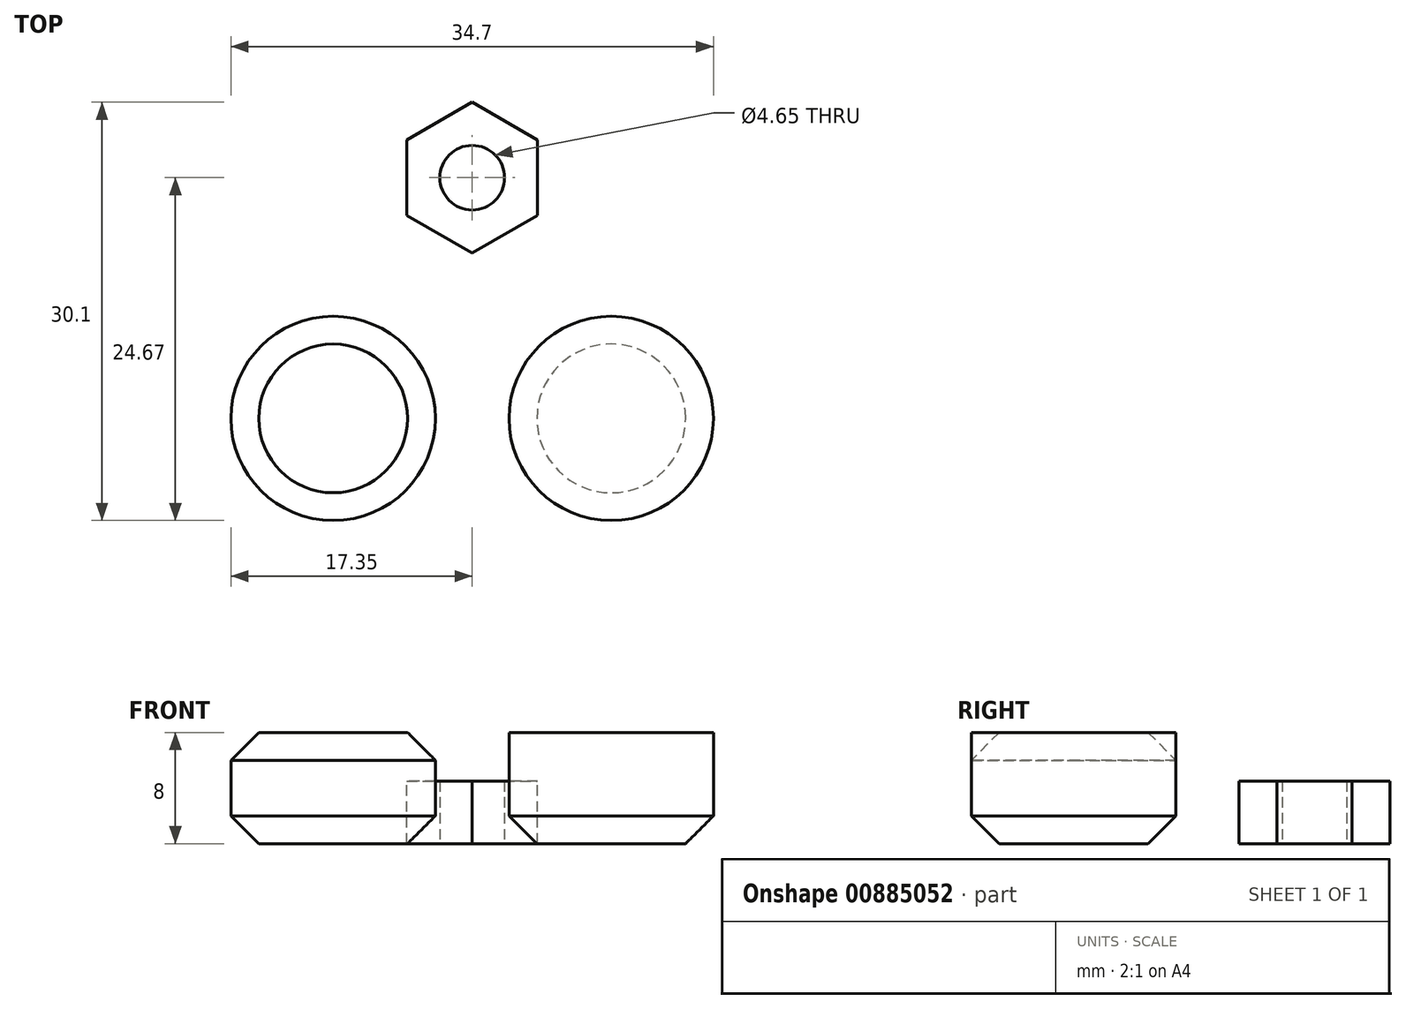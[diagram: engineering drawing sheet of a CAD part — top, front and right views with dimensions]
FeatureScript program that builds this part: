
annotation { "Feature Type Name" : "Feature", "Feature Type Description" : "" }
export const myFeature = defineFeature(function(context is Context, id is Id, definition is map)
    precondition{}
    {
        {
            var Q0;
            Q0=qCreatedBy(makeId("Top.planeOp"),FACE);
            var sketch = newSketch(context, id + "F0", { "sketchPlane" : qUnion([Q0])});
            skCircle(sketch, "E0", {"center": v(0, 0) * mm, "radius": 39 * mm});
            skCircle(sketch, "E1", {"center": v(0, 0) * mm, "radius": 2.33 * mm});
            skSolve(sketch);
        }
        {
            var Q0;
            Q0 = qSketchRegion(id + "F0", true);
            extrude(context, id + "F1", {"entities" : qUnion([Q0]), "endBound" : BoundingType.SYMMETRIC, "depth" : 8 * mm, "offsetDistance" : 25 * mm});
        }
        {
            var Q0;
            Q0=qCreatedBy(makeId("Right.planeOp"),FACE);
            var sketch = newSketch(context, id + "F2", { "sketchPlane" : qUnion([Q0])});
            skLineSegment(sketch, "E2", {"start": v(43.5, 0) * mm, "end": v(-48.07, 0) * mm, "construction": true});
            skLineSegment(sketch, "E3", {"start": v(-39, -4) * mm, "end": v(-39, 4) * mm, "construction": true});
            skCircle(sketch, "E4", {"center": v(-39, 0) * mm, "radius": 3 * mm});
            skSolve(sketch);
        }
        {
            var Q0;
            Q0 = qSketchRegion(id + "F2", true);
            var Q1;
            Q1=makeQuery(id+"F1.opExtrude","SWEPT_FACE",FACE,{"disambiguationData":[OSD([sQuery(id+"F0.wireOp",EDGE,"E1")])]});
            revolve(context, id + "F3", {"operationType" : NewBodyOperationType.REMOVE, "surfaceOperationType" : NewSurfaceOperationType.NEW, "entities" : qUnion([Q0]), "axis" : qUnion([Q1]), "revolveType" : RevolveType.FULL, "oppositeDirection" : true});
        }
        {
            var Q0;
            Q0=makeQuery(id+"F1.opExtrude","CAP_FACE",FACE,{"disambiguationData":[OSD([sQuery(id+"F0.wireOp",EDGE,"E0"),sQuery(id+"F0.wireOp",EDGE,"E1")])],"isStart":false});
            var sketch = newSketch(context, id + "F4", { "sketchPlane" : qUnion([Q0])});
            skCircle(sketch, "E5.cCircle", {"center": v(0, 0) * mm, "radius": 4.7 * mm, "construction": true});
            skLineSegment(sketch, "E5.0", {"start": v(-4.7, -2.71) * mm, "end": v(-4.7, 2.71) * mm});
            skLineSegment(sketch, "E5.1", {"start": v(-4.7, 2.71) * mm, "end": v(0, 5.43) * mm});
            skLineSegment(sketch, "E5.2", {"start": v(0, 5.43) * mm, "end": v(4.7, 2.71) * mm});
            skLineSegment(sketch, "E5.3", {"start": v(4.7, 2.71) * mm, "end": v(4.7, -2.71) * mm});
            skLineSegment(sketch, "E5.4", {"start": v(4.7, -2.71) * mm, "end": v(0, -5.43) * mm});
            skLineSegment(sketch, "E5.5", {"start": v(0, -5.43) * mm, "end": v(-4.7, -2.71) * mm});
            skPoint(sketch, "E5.0.midPoint", {"position": v(-4.7, 0) * mm});
            skSolve(sketch);
        }
        {
            var Q0;
            Q0=makeQuery(id+"F4.imprint","IMPRINT",FACE,{"disambiguationData":[TD([[makeQuery(id+"F4.imprint","IMPRINT",EDGE,{"derivedFrom":sQuery(id+"F4.wireOp",EDGE,"E5.0")}),-1.0]])]});
            extrude(context, id + "F5", {"entities" : qUnion([Q0]), "operationType" : NewBodyOperationType.REMOVE, "oppositeDirection" : true, "depth" : 3.5 * mm, "offsetDistance" : 25 * mm});
        }
        {
            var Q0;
            Q0=makeQuery(id+"F5.boolean.opBoolean","COPY",EDGE,{"derivedFrom":makeQuery(id+"F5.opExtrude","CAP_EDGE",EDGE,{"disambiguationData":[OSD([sQuery(id+"F4.wireOp",EDGE,"E5.2")])],"isStart":true})});
            var Q1;
            Q1=makeQuery(id+"F5.boolean.opBoolean","COPY",EDGE,{"derivedFrom":makeQuery(id+"F5.opExtrude","CAP_EDGE",EDGE,{"disambiguationData":[OSD([sQuery(id+"F4.wireOp",EDGE,"E5.3")])],"isStart":true})});
            var Q2;
            Q2=makeQuery(id+"F5.boolean.opBoolean","COPY",EDGE,{"derivedFrom":makeQuery(id+"F5.opExtrude","CAP_EDGE",EDGE,{"disambiguationData":[OSD([sQuery(id+"F4.wireOp",EDGE,"E5.4")])],"isStart":true})});
            var Q3;
            Q3=makeQuery(id+"F5.boolean.opBoolean","COPY",EDGE,{"derivedFrom":makeQuery(id+"F5.opExtrude","CAP_EDGE",EDGE,{"disambiguationData":[OSD([sQuery(id+"F4.wireOp",EDGE,"E5.5")])],"isStart":true})});
            var Q4;
            Q4=makeQuery(id+"F5.boolean.opBoolean","COPY",EDGE,{"derivedFrom":makeQuery(id+"F5.opExtrude","CAP_EDGE",EDGE,{"disambiguationData":[OSD([sQuery(id+"F4.wireOp",EDGE,"E5.0")])],"isStart":true})});
            var Q5;
            Q5=makeQuery(id+"F5.boolean.opBoolean","COPY",EDGE,{"derivedFrom":makeQuery(id+"F5.opExtrude","CAP_EDGE",EDGE,{"disambiguationData":[OSD([sQuery(id+"F4.wireOp",EDGE,"E5.1")])],"isStart":true})});
            var Q6;
            Q6=makeQuery(id+"F3.boolean.opBoolean","INTERSECT",EDGE,{"disambiguationData":[OD(1.0)],"derivedFrom":[makeQuery(id+"F1.opExtrude","SWEPT_FACE",FACE,{"disambiguationData":[OSD([sQuery(id+"F0.wireOp",EDGE,"E0")])]}),makeQuery(id+"F3.opRevolve","SWEPT_FACE",FACE,{"disambiguationData":[OSD([sQuery(id+"F2.wireOp",EDGE,"E4")])]})]});
            var Q7;
            Q7=makeQuery(id+"F3.boolean.opBoolean","INTERSECT",EDGE,{"disambiguationData":[OD(0.0)],"derivedFrom":[makeQuery(id+"F1.opExtrude","SWEPT_FACE",FACE,{"disambiguationData":[OSD([sQuery(id+"F0.wireOp",EDGE,"E0")])]}),makeQuery(id+"F3.opRevolve","SWEPT_FACE",FACE,{"disambiguationData":[OSD([sQuery(id+"F2.wireOp",EDGE,"E4")])]})]});
            chamfer(context, id + "F6", {"entities" : qUnion([Q0, Q1, Q2, Q3, Q4, Q5, Q6, Q7]), "width" : .5 * mm, "tangentPropagation" : true});
        }
        {
            var Q0;
            Q0=makeQuery(id+"F1.opExtrude","CAP_FACE",FACE,{"disambiguationData":[OSD([sQuery(id+"F0.wireOp",EDGE,"E0"),sQuery(id+"F0.wireOp",EDGE,"E1")])],"isStart":false});
            var sketch = newSketch(context, id + "F7", { "sketchPlane" : qUnion([Q0])});
            skCircle(sketch, "E6", {"center": v(-10, 17.32) * mm, "radius": 7.35 * mm});
            skLineSegment(sketch, "E7", {"start": v(0, -39) * mm, "end": v(0, 39) * mm, "construction": true});
            skLineSegment(sketch, "E8", {"start": v(39, 0) * mm, "end": v(-39, 0) * mm, "construction": true});
            skLineSegment(sketch, "E9", {"start": v(-2.6, -4.5) * mm, "end": v(19.5, 33.77) * mm, "construction": true});
            skLineSegment(sketch, "E10", {"start": v(2.6, -4.5) * mm, "end": v(-19.5, 33.77) * mm, "construction": true});
            skCircle(sketch, "E11", {"center": v(0, 0) * mm, "radius": 20 * mm, "construction": true});
            skCircle(sketch, "E12", {"center": v(-20, 0) * mm, "radius": 7.35 * mm});
            skCircle(sketch, "E13", {"center": v(10, 17.32) * mm, "radius": 7.35 * mm});
            skCircle(sketch, "E14", {"center": v(20, 0) * mm, "radius": 7.35 * mm});
            skCircle(sketch, "E15.MirrorC", {"center": v(10, -17.32) * mm, "radius": 7.35 * mm});
            skCircle(sketch, "E16.MirrorC", {"center": v(-10, -17.32) * mm, "radius": 7.35 * mm});
            skSolve(sketch);
        }
        {
            var Q0;
            Q0=makeQuery(id+"F7.imprint","IMPRINT",FACE,{"disambiguationData":[TD([[makeQuery(id+"F7.imprint","IMPRINT",EDGE,{"derivedFrom":sQuery(id+"F7.wireOp",EDGE,"E14")}),1.0]])]});
            var Q1;
            Q1=makeQuery(id+"F7.imprint","IMPRINT",FACE,{"disambiguationData":[TD([[makeQuery(id+"F7.imprint","IMPRINT",EDGE,{"derivedFrom":sQuery(id+"F7.wireOp",EDGE,"E15.MirrorC")}),-1.0]])]});
            var Q2;
            Q2=makeQuery(id+"F7.imprint","IMPRINT",FACE,{"disambiguationData":[TD([[makeQuery(id+"F7.imprint","IMPRINT",EDGE,{"derivedFrom":sQuery(id+"F7.wireOp",EDGE,"E16.MirrorC")}),-1.0]])]});
            var Q3;
            Q3=makeQuery(id+"F7.imprint","IMPRINT",FACE,{"disambiguationData":[TD([[makeQuery(id+"F7.imprint","IMPRINT",EDGE,{"derivedFrom":sQuery(id+"F7.wireOp",EDGE,"E12")}),1.0]])]});
            var Q4;
            Q4=makeQuery(id+"F7.imprint","IMPRINT",FACE,{"disambiguationData":[TD([[makeQuery(id+"F7.imprint","IMPRINT",EDGE,{"derivedFrom":sQuery(id+"F7.wireOp",EDGE,"E6")}),1.0]])]});
            var Q5;
            Q5=makeQuery(id+"F7.imprint","IMPRINT",FACE,{"disambiguationData":[TD([[makeQuery(id+"F7.imprint","IMPRINT",EDGE,{"derivedFrom":sQuery(id+"F7.wireOp",EDGE,"E13")}),1.0]])]});
            extrude(context, id + "F8", {"entities" : qUnion([Q0, Q1, Q2, Q3, Q4, Q5]), "operationType" : NewBodyOperationType.REMOVE, "oppositeDirection" : true, "depth" : 25 * mm, "offsetDistance" : 25 * mm});
        }
        {
            var Q0;
            Q0=makeQuery(id+"F8.boolean.opBoolean","COPY",EDGE,{"derivedFrom":makeQuery(id+"F8.opExtrude","CAP_EDGE",EDGE,{"disambiguationData":[OSD([sQuery(id+"F7.wireOp",EDGE,"E14")])],"isStart":true})});
            var Q1;
            Q1=makeQuery(id+"F8.boolean.opBoolean","COPY",EDGE,{"derivedFrom":makeQuery(id+"F8.opExtrude","CAP_EDGE",EDGE,{"disambiguationData":[OSD([sQuery(id+"F7.wireOp",EDGE,"E15.MirrorC")])],"isStart":true})});
            var Q2;
            Q2=makeQuery(id+"F8.boolean.opBoolean","COPY",EDGE,{"derivedFrom":makeQuery(id+"F8.opExtrude","CAP_EDGE",EDGE,{"disambiguationData":[OSD([sQuery(id+"F7.wireOp",EDGE,"E16.MirrorC")])],"isStart":true})});
            var Q3;
            Q3=makeQuery(id+"F8.boolean.opBoolean","COPY",EDGE,{"derivedFrom":makeQuery(id+"F8.opExtrude","CAP_EDGE",EDGE,{"disambiguationData":[OSD([sQuery(id+"F7.wireOp",EDGE,"E12")])],"isStart":true})});
            var Q4;
            Q4=makeQuery(id+"F8.boolean.opBoolean","COPY",EDGE,{"derivedFrom":makeQuery(id+"F8.opExtrude","CAP_EDGE",EDGE,{"disambiguationData":[OSD([sQuery(id+"F7.wireOp",EDGE,"E6")])],"isStart":true})});
            var Q5;
            Q5=makeQuery(id+"F8.boolean.opBoolean","COPY",EDGE,{"derivedFrom":makeQuery(id+"F8.opExtrude","CAP_EDGE",EDGE,{"disambiguationData":[OSD([sQuery(id+"F7.wireOp",EDGE,"E13")])],"isStart":true})});
            var Q6;
            Q6=makeQuery(id+"F8.boolean.opBoolean","INTERSECT",EDGE,{"derivedFrom":[makeQuery(id+"F1.opExtrude","CAP_FACE",FACE,{"disambiguationData":[OSD([sQuery(id+"F0.wireOp",EDGE,"E0"),sQuery(id+"F0.wireOp",EDGE,"E1")])],"isStart":true}),makeQuery(id+"F8.opExtrude","SWEPT_FACE",FACE,{"disambiguationData":[OSD([sQuery(id+"F7.wireOp",EDGE,"E12")])]})]});
            var Q7;
            Q7=makeQuery(id+"F8.boolean.opBoolean","INTERSECT",EDGE,{"derivedFrom":[makeQuery(id+"F1.opExtrude","CAP_FACE",FACE,{"disambiguationData":[OSD([sQuery(id+"F0.wireOp",EDGE,"E0"),sQuery(id+"F0.wireOp",EDGE,"E1")])],"isStart":true}),makeQuery(id+"F8.opExtrude","SWEPT_FACE",FACE,{"disambiguationData":[OSD([sQuery(id+"F7.wireOp",EDGE,"E16.MirrorC")])]})]});
            var Q8;
            Q8=makeQuery(id+"F8.boolean.opBoolean","INTERSECT",EDGE,{"derivedFrom":[makeQuery(id+"F1.opExtrude","CAP_FACE",FACE,{"disambiguationData":[OSD([sQuery(id+"F0.wireOp",EDGE,"E0"),sQuery(id+"F0.wireOp",EDGE,"E1")])],"isStart":true}),makeQuery(id+"F8.opExtrude","SWEPT_FACE",FACE,{"disambiguationData":[OSD([sQuery(id+"F7.wireOp",EDGE,"E15.MirrorC")])]})]});
            var Q9;
            Q9=makeQuery(id+"F8.boolean.opBoolean","INTERSECT",EDGE,{"derivedFrom":[makeQuery(id+"F1.opExtrude","CAP_FACE",FACE,{"disambiguationData":[OSD([sQuery(id+"F0.wireOp",EDGE,"E0"),sQuery(id+"F0.wireOp",EDGE,"E1")])],"isStart":true}),makeQuery(id+"F8.opExtrude","SWEPT_FACE",FACE,{"disambiguationData":[OSD([sQuery(id+"F7.wireOp",EDGE,"E14")])]})]});
            var Q10;
            Q10=makeQuery(id+"F8.boolean.opBoolean","INTERSECT",EDGE,{"derivedFrom":[makeQuery(id+"F1.opExtrude","CAP_FACE",FACE,{"disambiguationData":[OSD([sQuery(id+"F0.wireOp",EDGE,"E0"),sQuery(id+"F0.wireOp",EDGE,"E1")])],"isStart":true}),makeQuery(id+"F8.opExtrude","SWEPT_FACE",FACE,{"disambiguationData":[OSD([sQuery(id+"F7.wireOp",EDGE,"E13")])]})]});
            var Q11;
            Q11=makeQuery(id+"F8.boolean.opBoolean","INTERSECT",EDGE,{"derivedFrom":[makeQuery(id+"F1.opExtrude","CAP_FACE",FACE,{"disambiguationData":[OSD([sQuery(id+"F0.wireOp",EDGE,"E0"),sQuery(id+"F0.wireOp",EDGE,"E1")])],"isStart":true}),makeQuery(id+"F8.opExtrude","SWEPT_FACE",FACE,{"disambiguationData":[OSD([sQuery(id+"F7.wireOp",EDGE,"E6")])]})]});
            chamfer(context, id + "F9", {"entities" : qUnion([Q0, Q1, Q2, Q3, Q4, Q5, Q6, Q7, Q8, Q9, Q10, Q11]), "width" : 2 * mm, "tangentPropagation" : true});
        }
    });
